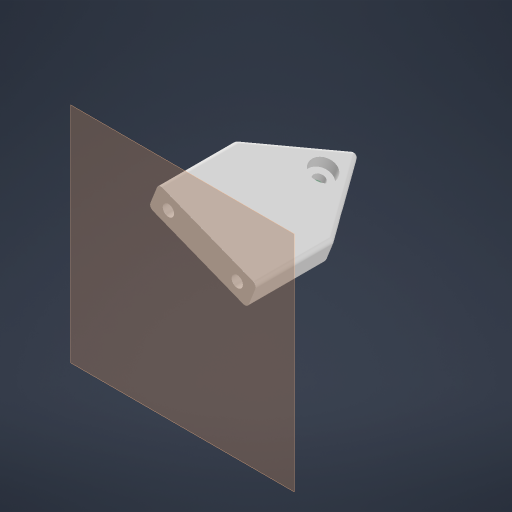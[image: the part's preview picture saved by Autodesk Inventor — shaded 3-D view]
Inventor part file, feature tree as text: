
AUTODESK INVENTOR PART (.ipt)
format: ipt  version: 2024.2 (Build 282272000, 272)  size: 361,984 bytes
history: native  units: in
note: dims shown in document units (in); Inventor stores cm internally (conversion verified against a paired STEP export)
features: sketch x10, extrude x4, other x3, plane x3, projected_geometry x2
ambient origin geometry x8: Origin, YZ Plane, XZ Plane, XY Plane, X Axis, Y Axis, Z Axis, Center Point
bodies: Solid1 (feature_tree)
feature tree (22):
  other  "Wheel_Axle_Holder.ipt"
  extrude  "Extrusion1"  Depth=0.3937in TaperAngle=0.0deg
  extrude  "Extrusion2"  TaperAngle=0.0deg  [1 undecoded]
  extrude  "Extrusion3"  [1 undecoded]
  extrude  "Extrusion4"  [1 undecoded]
  other  "Solid1::Wheel_Axle_Holder.ipt"
  other  "TaggingFeature1"
  sketch  "Sketch1"  dims[d0=0.3937in d1=1.0in d2=0.0in]
  sketch  "Sketch2"  dims[d3=1.0in d4=0.0in d5=0.0in d6=0.0in]
  sketch  "Sketch3"  dims[d7=1.0in d8=0.0in]
  sketch  "Sketch4"
  sketch  "Sketch5"
  sketch  "Sketch6"
  plane  "Work Plane1"
  plane  "Work Plane2"
  plane  "Work Plane3"
  sketch  "Sketch7"
  sketch  "Sketch8"
  sketch  "Sketch9"
  sketch  "Sketch10"
  projected_geometry  "Project Cut Edges1"
  projected_geometry  "Project Cut Edges2"
note: 3 required parameter values undecoded (feature->parameter linkage not recoverable at this tier; creation-order binding heuristic only, values carry confidence <= 0.55)
